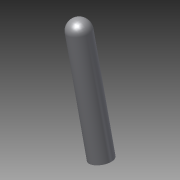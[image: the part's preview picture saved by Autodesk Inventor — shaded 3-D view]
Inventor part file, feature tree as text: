
AUTODESK INVENTOR PART (.ipt)
format: ipt  version: 2014 (Build 180170000, 170)  size: 96,256 bytes
history: native  units: in
note: dims shown in document units (in); Inventor stores cm internally (conversion verified against a paired STEP export)
features: other x14, revolve x1, sketch x1
ambient origin geometry x8: Origin, YZ Plane, XZ Plane, XY Plane, X Axis, Y Axis, Z Axis, Center Point
bodies: Solid1 (feature_tree)
feature tree (16):
  revolve  "Revolution1"  [1 undecoded]
  other  "rot_XY"
  other  "rot_YZ"
  other  "rot_ZX"
  other  "rot_X"
  other  "rot_Y"
  other  "rot_Z"
  other  "rot_Center"
  other  "to_cap_XY"
  other  "to_cap_YZ"
  other  "to_cap_ZX"
  other  "to_cap_X"
  other  "to_cap_Y"
  other  "to_cap_Z"
  other  "to_cap_Center"
  sketch  "Sketch_1"  dims[d0=360.0deg]
note: 1 required parameter value undecoded (feature->parameter linkage not recoverable at this tier; creation-order binding heuristic only, values carry confidence <= 0.55)
